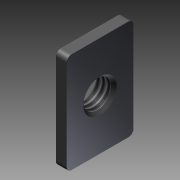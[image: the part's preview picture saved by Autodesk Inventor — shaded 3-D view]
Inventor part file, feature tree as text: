
AUTODESK INVENTOR PART (.ipt)
format: ipt  version: 2016 SP1 (Build 200210100, 210)  size: 119,808 bytes
history: native  units: mm
features: other x7, sketch x3, revolve x2, extrude x1, thread x1
ambient origin geometry x8: Origin, YZ Plane, XZ Plane, XY Plane, X Axis, Y Axis, Z Axis, Center Point
bodies: Solid1 (feature_tree)
feature tree (14):
  extrude  "Extrusion1"  TaperAngle=360.0deg  [1 undecoded]
  revolve  "Revolution1"  [1 undecoded]
  revolve  "Revolution2"  [1 undecoded]
  thread  "Thread1"  [1 undecoded]
  other  "dummy_XY"
  other  "dummy_YZ"
  other  "dummy_ZX"
  other  "dummy_X"
  other  "dummy_Y"
  other  "dummy_Z"
  other  "dummy_Center"
  sketch  "Sketch_1"  dims[d0=3.0mm d1=0.0mm d2=360.0deg]
  sketch  "Sketch_2"  dims[d3=360.0deg d4=2.134mm d5=0.0mm]
  sketch  "Sketch_3"
note: 4 required parameter values undecoded (feature->parameter linkage not recoverable at this tier; creation-order binding heuristic only, values carry confidence <= 0.55)